# Revit family: SiouxChief_FloorDrain_HALO_822-3D_R9 Side Outlet_Round
name_source: partatom
category: Plumbing Fixtures
units: mm (PartAtom-declared; Revit-internal decimal feet)

## family parameters
Cut with Voids When Loaded = No
Host = Face
Part Type = Normal
Room Calculation Point = No
Round Connector Dimension = Use Radius
Shared = No

## types (1)
- 822-3D_R9
    2" Side Outlet Visibility = No
    3" Side Outlet Visibility = Yes
    Connection Radius = 0' - 1 1/2"
    Default Elevation = 0' - 0"
    Description = Halo Base w/Flange / Head / Strainer - 3" Side Outlet No-Hub
    F = 0' - 0 3/8"
    Hub Offset = 0' - 4 1/4"
    Inside Hub Offset = 0' - 1 1/4"
    Manufacturer = Sioux Chief Manufacturing
    Model = 822-3D_R9
    Omni Class 23 Code = 23.70.50.21.24
    Omni Class 23 Title = Waste Water Drains
    Outlet Diameter = 0' - 3 1/2"
    R = 0' - 0 3/4"
    URL = www.siouxchief.com

## geometry (parser evidence)
native form markers: Sweep x15
no freeform markers — native parametric forms only
